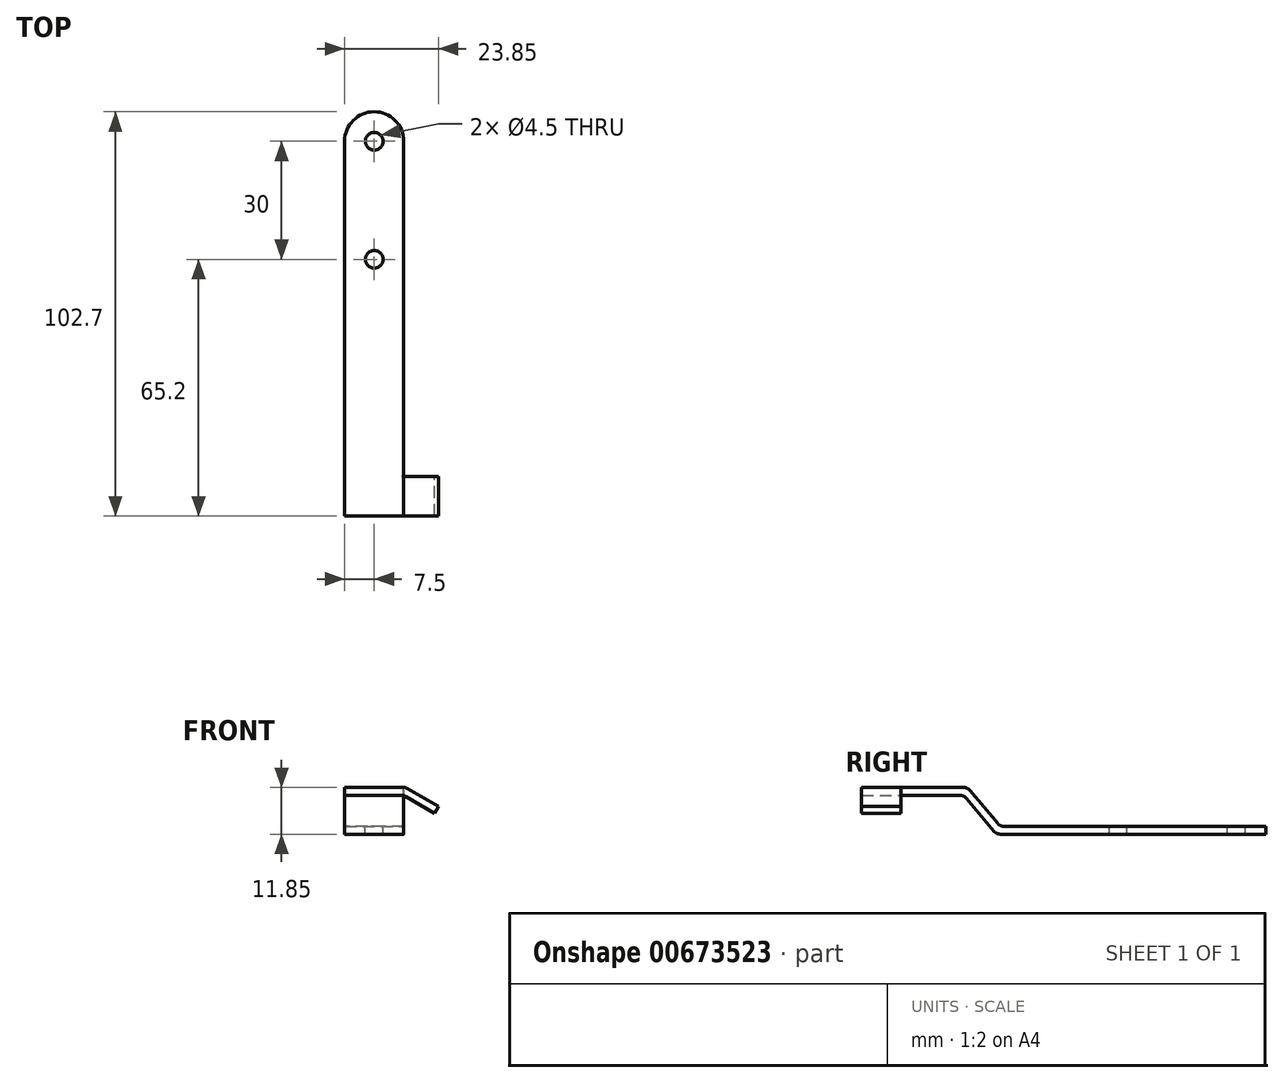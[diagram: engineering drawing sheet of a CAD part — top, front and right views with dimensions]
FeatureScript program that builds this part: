
annotation { "Feature Type Name" : "Feature", "Feature Type Description" : "" }
export const myFeature = defineFeature(function(context is Context, id is Id, definition is map)
    precondition{}
    {
        {
            var Q0;
            Q0=qCreatedBy(makeId("Top.planeOp"),FACE);
            var sketch = newSketch(context, id + "F0", { "sketchPlane" : qUnion([Q0])});
            skLineSegment(sketch, "E0", {"start": v(-7.5, 0) * mm, "end": v(-7.5, 60) * mm});
            skLineSegment(sketch, "E1", {"start": v(7.5, 0) * mm, "end": v(7.5, 60) * mm});
            skArc(sketch, "E2", {"start": v(7.5, 60) * mm, "mid": v(0, 67.5) * mm, "end": v(-7.5, 60) * mm});
            skLineSegment(sketch, "E3", {"start": v(-7.5, 0) * mm, "end": v(7.5, 0) * mm});
            skSolve(sketch);
        }
        {
            var Q0;
            Q0=makeQuery(id+"F0.imprint","IMPRINT",FACE,{"disambiguationData":[TD([[makeQuery(id+"F0.imprint","IMPRINT",EDGE,{"derivedFrom":sQuery(id+"F0.wireOp",EDGE,"E0")}),-1.0]])]});
            extrude(context, id + "F1", {"entities" : qUnion([Q0]), "depth" : 2 * mm, "offsetDistance" : 25 * mm});
        }
        {
            var Q0;
            Q0=makeQuery(id+"F1.opExtrude","SWEPT_FACE",FACE,{"disambiguationData":[OSD([sQuery(id+"F0.wireOp",EDGE,"E1")])]});
            var sketch = newSketch(context, id + "F2", { "sketchPlane" : qUnion([Q0])});
            skLineSegment(sketch, "E4", {"start": v(-1.53, 0.71) * mm, "end": v(-9.2, 9.85) * mm});
            skLineSegment(sketch, "E5", {"start": v(-7.67, 11.14) * mm, "end": v(0, 2) * mm});
            skArc(sketch, "E6", {"start": v(-1.53, 0.71) * mm, "mid": v(-0.85, 0.19) * mm, "end": v(0, 0) * mm});
            skLineSegment(sketch, "E7", {"start": v(0, 2) * mm, "end": v(0, 0) * mm});
            skLineSegment(sketch, "E8", {"start": v(-9.2, 9.85) * mm, "end": v(-9.2, 11.85) * mm});
            skArc(sketch, "E9", {"start": v(-7.67, 11.14) * mm, "mid": v(-8.35, 11.66) * mm, "end": v(-9.2, 11.85) * mm});
            skSolve(sketch);
        }
        {
            var Q0;
            Q0 = qSketchRegion(id + "F2", true);
            var Q1;
            Q1=makeQuery(id+"F1.opExtrude","SWEPT_FACE",FACE,{"disambiguationData":[OSD([sQuery(id+"F0.wireOp",EDGE,"E0")])]});
            extrude(context, id + "F3", {"entities" : qUnion([Q0]), "operationType" : NewBodyOperationType.ADD, "endBound" : BoundingType.UP_TO_SURFACE, "oppositeDirection" : true, "depth" : 25 * mm, "endBoundEntityFace" : qUnion([Q1]), "offsetDistance" : 25 * mm});
        }
        {
            var Q0;
            Q0=makeQuery(id+"F1.opExtrude","CAP_FACE",FACE,{"disambiguationData":[OSD([sQuery(id+"F0.wireOp",EDGE,"E0"),sQuery(id+"F0.wireOp",EDGE,"E1"),sQuery(id+"F0.wireOp",EDGE,"E2"),sQuery(id+"F0.wireOp",EDGE,"E3")])],"isStart":false});
            var sketch = newSketch(context, id + "F4", { "sketchPlane" : qUnion([Q0])});
            skLineSegment(sketch, "E10", {"start": v(-7.5, -7.67) * mm, "end": v(-7.5, -43.84) * mm});
            skLineSegment(sketch, "E11", {"start": v(-7.5, -43.84) * mm, "end": v(7.5, -43.84) * mm});
            skLineSegment(sketch, "E12", {"start": v(7.5, -43.84) * mm, "end": v(7.5, -7.67) * mm});
            skLineSegment(sketch, "E13", {"start": v(-7.5, -7.67) * mm, "end": v(7.5, -7.67) * mm});
            skSolve(sketch);
        }
        {
            var Q0;
            Q0 = qSketchRegion(id + "F4", true);
            extrude(context, id + "F5", {"entities" : qUnion([Q0]), "depth" : 2 * mm, "offsetDistance" : 25 * mm});
        }
        {
            var Q0;
            {var subQ0=sQuery(id+"F0.wireOp",EDGE,"E0");Q0=makeQuery(id+"F3.boolean.opBoolean","MERGE",FACE,{"derivedFrom":[makeQuery(id+"F1.opExtrude","SWEPT_FACE",FACE,{"disambiguationData":[OSD([subQ0])]}),makeQuery(id+"F3.opExtrude","CAP_FACE",FACE,{"disambiguationData":[OSD([subQ0])],"isStart":false})]});}
            var sketch = newSketch(context, id + "F6", { "sketchPlane" : qUnion([Q0])});
            skLineSegment(sketch, "E14", {"start": v(9.2, 9.85) * mm, "end": v(25.2, 9.85) * mm});
            skLineSegment(sketch, "E15", {"start": v(25.2, 11.85) * mm, "end": v(9.2, 11.85) * mm});
            skLineSegment(sketch, "E16", {"start": v(9.2, 11.85) * mm, "end": v(9.2, 9.85) * mm});
            skLineSegment(sketch, "E17", {"start": v(25.2, 11.85) * mm, "end": v(25.2, 9.85) * mm});
            skSolve(sketch);
        }
        {
            var Q0;
            Q0 = qSketchRegion(id + "F6", true);
            var Q1;
            Q1=makeQuery(id+"F3.boolean.opBoolean","MERGE",FACE,{"derivedFrom":[makeQuery(id+"F1.opExtrude","SWEPT_FACE",FACE,{"disambiguationData":[OSD([sQuery(id+"F0.wireOp",EDGE,"E1")])]}),makeQuery(id+"F3.opExtrude","CAP_FACE",FACE,{"disambiguationData":[OSD([sQuery(id+"F2.wireOp",EDGE,"E4"),sQuery(id+"F2.wireOp",EDGE,"BXSzwJhY-Sn16-FGPY-2YO3-YHpVwpTB8mmX"),sQuery(id+"F2.wireOp",EDGE,"E5"),sQuery(id+"F2.wireOp",EDGE,"ABKbyi1K-y6FW-3vUi-oPL1-ZAWxRmIaJKqp")])],"isStart":true})]});
            extrude(context, id + "F7", {"entities" : qUnion([Q0]), "operationType" : NewBodyOperationType.ADD, "endBound" : BoundingType.UP_TO_SURFACE, "oppositeDirection" : true, "depth" : 25 * mm, "endBoundEntityFace" : qUnion([Q1]), "offsetDistance" : 25 * mm});
        }
        {
            var Q0;
            Q0=makeQuery(id+"F3.boolean.opBoolean","MERGE",EDGE,{"derivedFrom":[makeQuery(id+"F1.opExtrude","CAP_EDGE",EDGE,{"disambiguationData":[OSD([sQuery(id+"F0.wireOp",EDGE,"E3")])],"isStart":true}),makeQuery(id+"F3.opExtrude","SWEPT_EDGE",EDGE,{"disambiguationData":[OSD([sQuery(id+"F0.wireOp",EDGE,"E1"),sQuery(id+"F2.wireOp",EDGE,"E4"),sQuery(id+"F2.wireOp",EDGE,"ABKbyi1K-y6FW-3vUi-oPL1-ZAWxRmIaJKqp")])]})]});
            var Q1;
            Q1=makeQuery(id+"F3.boolean.opBoolean","MERGE",EDGE,{"derivedFrom":[makeQuery(id+"F1.opExtrude","CAP_EDGE",EDGE,{"disambiguationData":[OSD([sQuery(id+"F0.wireOp",EDGE,"E3")])],"isStart":false}),makeQuery(id+"F3.opExtrude","SWEPT_EDGE",EDGE,{"disambiguationData":[OSD([sQuery(id+"F0.wireOp",EDGE,"E1"),sQuery(id+"F2.wireOp",EDGE,"E5"),sQuery(id+"F2.wireOp",EDGE,"ABKbyi1K-y6FW-3vUi-oPL1-ZAWxRmIaJKqp")])]})]});
            var Q2;
            {var subQ0=sQuery(id+"F2.wireOp",EDGE,"E5");Q2=makeQuery(id+"F7.boolean.opBoolean","MERGE",EDGE,{"derivedFrom":[makeQuery(id+"F3.opExtrude","SWEPT_EDGE",EDGE,{"disambiguationData":[OSD([sQuery(id+"F2.wireOp",EDGE,"BXSzwJhY-Sn16-FGPY-2YO3-YHpVwpTB8mmX"),subQ0])]}),makeQuery(id+"F7.opExtrude","SWEPT_EDGE",EDGE,{"disambiguationData":[OSD([sQuery(id+"F0.wireOp",EDGE,"E0"),subQ0,sQuery(id+"F6.wireOp",EDGE,"E15"),sQuery(id+"F6.wireOp",EDGE,"E16")])]})]});}
            var Q3;
            {var subQ0=sQuery(id+"F2.wireOp",EDGE,"E4");Q3=makeQuery(id+"F7.boolean.opBoolean","MERGE",EDGE,{"derivedFrom":[makeQuery(id+"F3.opExtrude","SWEPT_EDGE",EDGE,{"disambiguationData":[OSD([subQ0,sQuery(id+"F2.wireOp",EDGE,"BXSzwJhY-Sn16-FGPY-2YO3-YHpVwpTB8mmX")])]}),makeQuery(id+"F7.opExtrude","SWEPT_EDGE",EDGE,{"disambiguationData":[OSD([sQuery(id+"F0.wireOp",EDGE,"E0"),subQ0,sQuery(id+"F6.wireOp",EDGE,"E14"),sQuery(id+"F6.wireOp",EDGE,"E16")])]})]});}
            fillet(context, id + "F8", {"entities" : qUnion([Q0, Q1, Q2, Q3]), "radius" : 2 * mm, "tangentPropagation" : true, "allowEdgeOverflow" : false});
        }
        {
            var Q0;
            Q0=makeQuery(id+"F5.opExtrude","SWEPT_BODY",BODY,{"disambiguationData":[OSD([sQuery(id+"F4.wireOp",EDGE,"E10"),sQuery(id+"F4.wireOp",EDGE,"E11"),sQuery(id+"F4.wireOp",EDGE,"E12"),sQuery(id+"F4.wireOp",EDGE,"E13")])]});
            deleteBodies(context, id + "F9", {"entities" : qUnion([Q0])});
        }
        {
            var Q0;
            Q0=makeQuery(id+"F7.opExtrude","SWEPT_FACE",FACE,{"disambiguationData":[OSD([sQuery(id+"F6.wireOp",EDGE,"E17")])]});
            var sketch = newSketch(context, id + "F10", { "sketchPlane" : qUnion([Q0])});
            skLineSegment(sketch, "E18", {"start": v(7.5, 9.85) * mm, "end": v(15.35, 5.32) * mm});
            skLineSegment(sketch, "E19", {"start": v(15.35, 5.32) * mm, "end": v(16.35, 7.05) * mm});
            skLineSegment(sketch, "E20", {"start": v(-7.5, 11.85) * mm, "end": v(7.5, 11.85) * mm});
            skLineSegment(sketch, "E21", {"start": v(-7.5, 9.85) * mm, "end": v(7.5, 9.85) * mm});
            skLineSegment(sketch, "E22", {"start": v(-7.5, 11.85) * mm, "end": v(-7.5, 9.85) * mm});
            skLineSegment(sketch, "E23", {"start": v(16.35, 7.05) * mm, "end": v(8.38, 11.65) * mm});
            skArc(sketch, "E24", {"start": v(8.38, 11.65) * mm, "mid": v(7.96, 11.82) * mm, "end": v(7.5, 11.85) * mm});
            skSolve(sketch);
        }
        {
            var Q0;
            Q0 = qSketchRegion(id + "F10", true);
            extrude(context, id + "F11", {"entities" : qUnion([Q0]), "operationType" : NewBodyOperationType.ADD, "depth" : 10 * mm, "offsetDistance" : 25 * mm});
        }
        {
            var Q0;
            Q0=makeQuery(id+"F1.opExtrude","CAP_FACE",FACE,{"disambiguationData":[OSD([sQuery(id+"F0.wireOp",EDGE,"E0"),sQuery(id+"F0.wireOp",EDGE,"E1"),sQuery(id+"F0.wireOp",EDGE,"E2"),sQuery(id+"F0.wireOp",EDGE,"E3")])],"isStart":false});
            var sketch = newSketch(context, id + "F12", { "sketchPlane" : qUnion([Q0])});
            skCircle(sketch, "E25", {"center": v(0, 60) * mm, "radius": 2.25 * mm});
            skCircle(sketch, "E26", {"center": v(0, 30) * mm, "radius": 2.25 * mm});
            skSolve(sketch);
        }
        {
            var Q0;
            Q0 = qSketchRegion(id + "F12", true);
            extrude(context, id + "F13", {"entities" : qUnion([Q0]), "operationType" : NewBodyOperationType.REMOVE, "oppositeDirection" : true, "depth" : 25 * mm, "offsetDistance" : 25 * mm});
        }
        {
            var Q0;
            Q0=makeQuery(id+"F11.opExtrude","SWEPT_EDGE",EDGE,{"disambiguationData":[OSD([sQuery(id+"F0.wireOp",EDGE,"E1"),sQuery(id+"F2.wireOp",EDGE,"E4"),sQuery(id+"F2.wireOp",EDGE,"E5"),sQuery(id+"F2.wireOp",EDGE,"E6"),sQuery(id+"F2.wireOp",EDGE,"E7"),sQuery(id+"F2.wireOp",EDGE,"E8"),sQuery(id+"F2.wireOp",EDGE,"E9"),sQuery(id+"F6.wireOp",EDGE,"E17"),sQuery(id+"F10.wireOp",EDGE,"E18"),sQuery(id+"F10.wireOp",EDGE,"E21")])]});
            fillet(context, id + "F14", {"entities" : qUnion([Q0]), "radius" : 2 * mm, "tangentPropagation" : true, "allowEdgeOverflow" : false});
        }
    });
